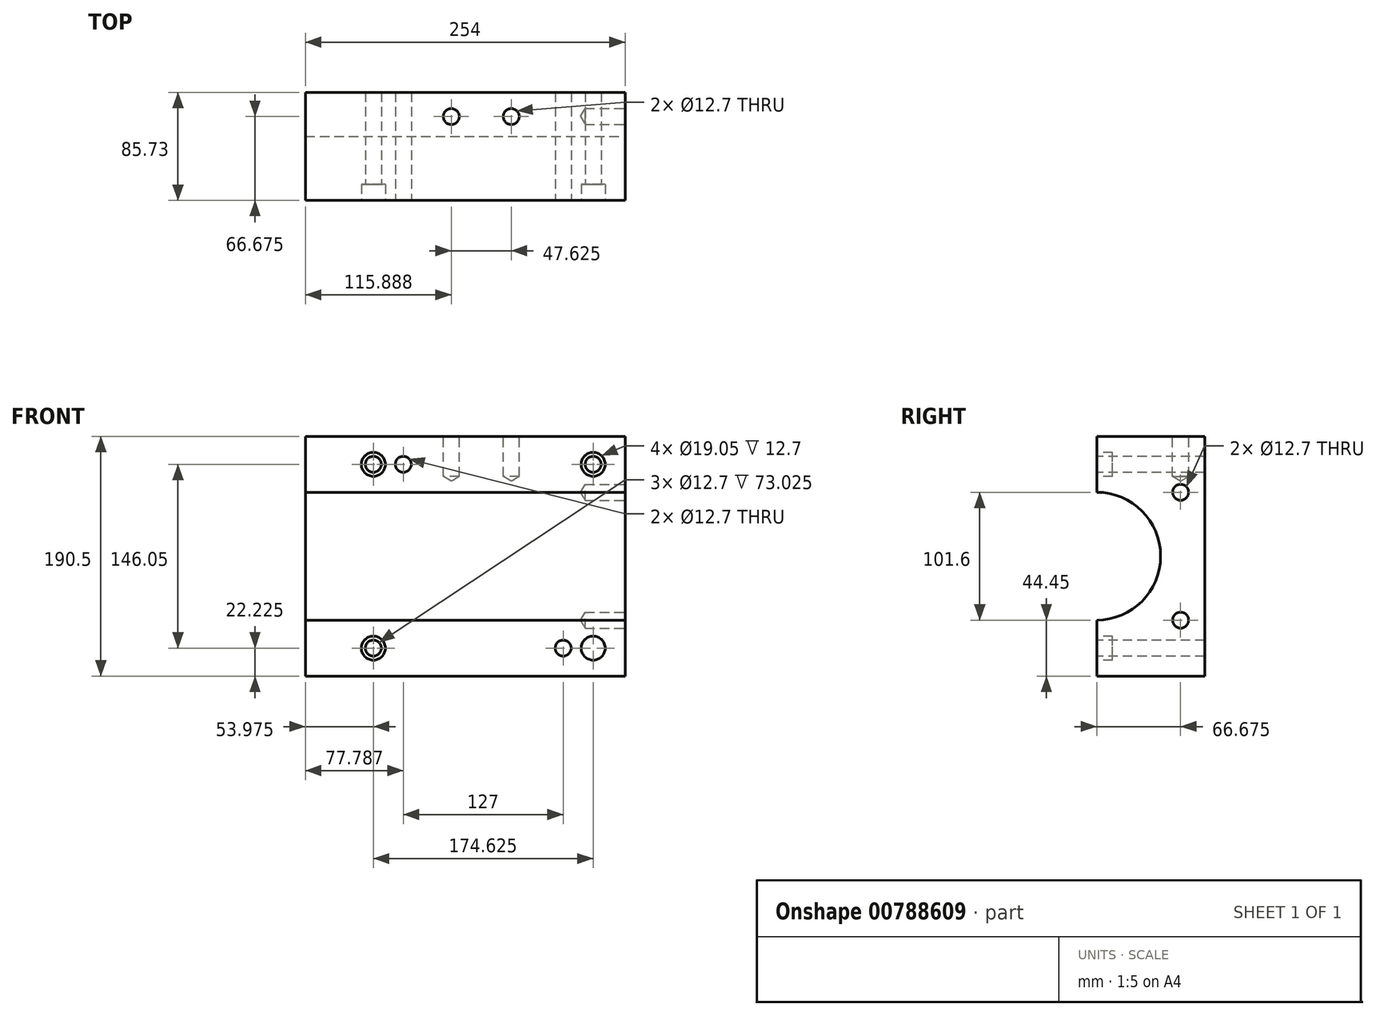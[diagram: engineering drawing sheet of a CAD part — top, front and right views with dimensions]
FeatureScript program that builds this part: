
annotation { "Feature Type Name" : "Feature", "Feature Type Description" : "" }
export const myFeature = defineFeature(function(context is Context, id is Id, definition is map)
    precondition{}
    {
        {
            var Q0;
            Q0=qCreatedBy(makeId("Front.planeOp"),FACE);
            var sketch = newSketch(context, id + "F0", { "sketchPlane" : qUnion([Q0])});
            skLineSegment(sketch, "E0.bottom", {"start": v(-127, 95.25) * mm, "end": v(127, 95.25) * mm});
            skLineSegment(sketch, "E0.top", {"start": v(-127, -95.25) * mm, "end": v(127, -95.25) * mm});
            skLineSegment(sketch, "E0.left", {"start": v(-127, 95.25) * mm, "end": v(-127, -95.25) * mm});
            skLineSegment(sketch, "E0.right", {"start": v(127, 95.25) * mm, "end": v(127, -95.25) * mm});
            skPoint(sketch, "E0.middle", {"position": v(0, 0) * mm});
            skSolve(sketch);
        }
        {
            var Q0;
            Q0 = qSketchRegion(id + "F0", true);
            extrude(context, id + "F1", {"entities" : qUnion([Q0]), "oppositeDirection" : true, "depth" : 85.72 * mm, "offsetDistance" : 25.4 * mm});
        }
        {
            var Q0;
            Q0=qCreatedBy(makeId("Right.planeOp"),FACE);
            var sketch = newSketch(context, id + "F2", { "sketchPlane" : qUnion([Q0])});
            skArc(sketch, "E1", {"start": v(0, -50.8) * mm, "mid": v(50.8, 0) * mm, "end": v(0, 50.8) * mm});
            skLineSegment(sketch, "E2", {"start": v(0, 0) * mm, "end": v(0, 50.8) * mm});
            skLineSegment(sketch, "E3", {"start": v(0, 0) * mm, "end": v(0, -50.8) * mm});
            skSolve(sketch);
        }
        {
            var Q0;
            Q0 = qSketchRegion(id + "F2", true);
            extrude(context, id + "F3", {"entities" : qUnion([Q0]), "operationType" : NewBodyOperationType.REMOVE, "endBound" : BoundingType.SYMMETRIC, "oppositeDirection" : true, "depth" : 254 * mm, "offsetDistance" : 25.4 * mm});
        }
        {
            var Q0;
            {var subQ0=sQuery(id+"F0.wireOp",EDGE,"E0.bottom");var subQ1=sQuery(id+"F0.wireOp",EDGE,"E0.right");var subQ2=sQuery(id+"F0.wireOp",EDGE,"E0.left");Q0=makeQuery(id+"F3.boolean.opBoolean","SPLIT",FACE,{"disambiguationData":[TD([makeQuery(id+"F1.opExtrude","SWEPT_FACE",FACE,{"disambiguationData":[OSD([subQ0])]})])],"derivedFrom":makeQuery(id+"F1.opExtrude","CAP_FACE",FACE,{"disambiguationData":[OSD([subQ0,sQuery(id+"F0.wireOp",EDGE,"E0.top"),subQ2,subQ1])],"isStart":true})});}
            var sketch = newSketch(context, id + "F4", { "sketchPlane" : qUnion([Q0])});
            skLineSegment(sketch, "E4", {"start": v(-127, 73.02) * mm, "end": v(-73.02, 73.02) * mm, "construction": true});
            skCircle(sketch, "E5", {"center": v(-73.02, 73.02) * mm, "radius": 9.53 * mm});
            skLineSegment(sketch, "E6", {"start": v(-73.02, 73.02) * mm, "end": v(-73.02, 95.25) * mm, "construction": true});
            skLineSegment(sketch, "E7", {"start": v(0, 0) * mm, "end": v(0, 137.12) * mm, "construction": true});
            skPoint(sketch, "E7.endSnap0", {"position": v(0, 50.8) * mm});
            skLineSegment(sketch, "E8", {"start": v(0, 0) * mm, "end": v(220.34, 0) * mm, "construction": true});
            skLineSegment(sketch, "E9", {"start": v(0, 0) * mm, "end": v(-211.05, 0) * mm, "construction": true});
            skLineSegment(sketch, "E10", {"start": v(0, 0) * mm, "end": v(0, -119.32) * mm, "construction": true});
            skCircle(sketch, "E11.MirrorC", {"center": v(-73.02, -73.02) * mm, "radius": 9.53 * mm});
            skLineSegment(sketch, "E12", {"start": v(127, 73.02) * mm, "end": v(111.13, 73.02) * mm, "construction": true});
            skCircle(sketch, "E13", {"center": v(101.6, 73.02) * mm, "radius": 9.53 * mm});
            skCircle(sketch, "E14.MirrorC", {"center": v(101.6, -73.02) * mm, "radius": 9.53 * mm});
            skSolve(sketch);
        }
        {
            var Q0;
            Q0 = qSketchRegion(id + "F4", true);
            extrude(context, id + "F5", {"entities" : qUnion([Q0]), "operationType" : NewBodyOperationType.REMOVE, "oppositeDirection" : true, "depth" : 12.7 * mm, "offsetDistance" : 25.4 * mm});
        }
        {
            var Q0;
            {var subQ0=sQuery(id+"F0.wireOp",EDGE,"E0.bottom");var subQ1=sQuery(id+"F0.wireOp",EDGE,"E0.right");var subQ2=sQuery(id+"F0.wireOp",EDGE,"E0.left");Q0=makeQuery(id+"F3.boolean.opBoolean","SPLIT",FACE,{"disambiguationData":[TD([makeQuery(id+"F1.opExtrude","SWEPT_FACE",FACE,{"disambiguationData":[OSD([subQ0])]})])],"derivedFrom":makeQuery(id+"F1.opExtrude","CAP_FACE",FACE,{"disambiguationData":[OSD([subQ0,sQuery(id+"F0.wireOp",EDGE,"E0.top"),subQ2,subQ1])],"isStart":true})});}
            var sketch = newSketch(context, id + "F6", { "sketchPlane" : qUnion([Q0])});
            skCircle(sketch, "E15", {"center": v(-49.21, 73.02) * mm, "radius": 6.35 * mm});
            skPoint(sketch, "E16.start.orphan", {"position": v(101.6, 73.02) * mm});
            skLineSegment(sketch, "E17", {"start": v(0, 0) * mm, "end": v(215.97, 0) * mm});
            skCircle(sketch, "E18.MirrorC", {"center": v(77.79, -73.02) * mm, "radius": 6.35 * mm});
            skSolve(sketch);
        }
        {
            var Q0;
            Q0 = qSketchRegion(id + "F6", true);
            extrude(context, id + "F7", {"entities" : qUnion([Q0]), "operationType" : NewBodyOperationType.REMOVE, "endBound" : BoundingType.UP_TO_NEXT, "oppositeDirection" : true, "depth" : 25.4 * mm, "offsetDistance" : 25.4 * mm});
        }
        {
            var Q0;
            Q0=makeQuery(id+"F5.boolean.opBoolean","COPY",FACE,{"derivedFrom":makeQuery(id+"F5.opExtrude","CAP_FACE",FACE,{"disambiguationData":[OSD([sQuery(id+"F4.wireOp",EDGE,"E5")])],"isStart":false})});
            var sketch = newSketch(context, id + "F8", { "sketchPlane" : qUnion([Q0])});
            skCircle(sketch, "E19", {"center": v(-73.02, 73.02) * mm, "radius": 6.35 * mm});
            skLineSegment(sketch, "E20", {"start": v(0, 0) * mm, "end": v(0, 114.26) * mm, "construction": true});
            skLineSegment(sketch, "E21", {"start": v(0, 0) * mm, "end": v(0, -112.48) * mm, "construction": true});
            skLineSegment(sketch, "E22", {"start": v(0, 0) * mm, "end": v(-162.05, 0) * mm, "construction": true});
            skLineSegment(sketch, "E23", {"start": v(0, 0) * mm, "end": v(231.12, 0) * mm, "construction": true});
            skCircle(sketch, "E24.MirrorC", {"center": v(-73.02, -73.02) * mm, "radius": 6.35 * mm});
            skSolve(sketch);
        }
        {
            var Q0;
            Q0=makeQuery(id+"F5.boolean.opBoolean","COPY",FACE,{"derivedFrom":makeQuery(id+"F5.opExtrude","CAP_FACE",FACE,{"disambiguationData":[OSD([sQuery(id+"F4.wireOp",EDGE,"E13")])],"isStart":false})});
            var sketch = newSketch(context, id + "F9", { "sketchPlane" : qUnion([Q0])});
            skCircle(sketch, "E25", {"center": v(101.6, 73.02) * mm, "radius": 6.35 * mm});
            skLineSegment(sketch, "E26", {"start": v(0, 0) * mm, "end": v(190.85, 0) * mm});
            skCircle(sketch, "E27.MirrorC", {"center": v(101.6, -73.02) * mm, "radius": 6.35 * mm});
            skSolve(sketch);
        }
        {
            var Q0;
            Q0 = qSketchRegion(id + "F8", true);
            var Q1;
            Q1=makeQuery(id+"F9.imprint","IMPRINT",FACE,{"disambiguationData":[TD([[makeQuery(id+"F9.imprint","IMPRINT",EDGE,{"derivedFrom":sQuery(id+"F9.wireOp",EDGE,"E25")}),1.0]])]});
            var Q2;
            Q2=makeQuery(id+"F9.imprint","IMPRINT",FACE,{"disambiguationData":[TD([[makeQuery(id+"F9.imprint","IMPRINT",EDGE,{"derivedFrom":sQuery(id+"F9.wireOp",EDGE,"E27.MirrorC")}),-1.0]])]});
            extrude(context, id + "F10", {"entities" : qUnion([Q0, Q1, Q2]), "operationType" : NewBodyOperationType.REMOVE, "oppositeDirection" : true, "depth" : 82.55 * mm, "offsetDistance" : 25.4 * mm});
        }
        {
            var Q0;
            Q0=makeQuery(id+"F1.opExtrude","SWEPT_FACE",FACE,{"disambiguationData":[OSD([sQuery(id+"F0.wireOp",EDGE,"E0.bottom")])]});
            var sketch = newSketch(context, id + "F11", { "sketchPlane" : qUnion([Q0])});
            skLineSegment(sketch, "E28", {"start": v(-127, 85.73) * mm, "end": v(-127, 76.2) * mm, "construction": true});
            skLineSegment(sketch, "E29", {"start": v(-127, 76.2) * mm, "end": v(-33.34, 76.2) * mm, "construction": true});
            skLineSegment(sketch, "E30", {"start": v(-33.34, 76.2) * mm, "end": v(-11.11, 76.2) * mm, "construction": true});
            skLineSegment(sketch, "E31", {"start": v(-11.11, 76.2) * mm, "end": v(-11.11, 66.68) * mm, "construction": true});
            skLineSegment(sketch, "E32", {"start": v(127, 85.73) * mm, "end": v(127, 76.2) * mm});
            skLineSegment(sketch, "E33", {"start": v(-11.11, 66.68) * mm, "end": v(36.51, 66.68) * mm, "construction": true});
            skSolve(sketch);
        }
        {
            var Q0;
            Q0=sQuery(id+"F11.wireOp",VERTEX,"E31.end");
            var Q1;
            Q1=sQuery(id+"F11.wireOp",VERTEX,"E33.end");
            var Q2;
            Q2=makeQuery(id+"F1.opExtrude","SWEPT_BODY",BODY,{"disambiguationData":[OSD([sQuery(id+"F0.wireOp",EDGE,"E0.bottom"),sQuery(id+"F0.wireOp",EDGE,"E0.top"),sQuery(id+"F0.wireOp",EDGE,"E0.left"),sQuery(id+"F0.wireOp",EDGE,"E0.right")])]});
            hole(context, id + "F12", {"style" : HoleStyle.SIMPLE, "endStyle" : HoleEndStyle.BLIND, "holeDiameter" : 12.7 * mm, "majorDiameter" : 5 * mm, "holeDepth" : 31.75 * mm, "isTappedThrough" : true, "tappedDepth" : 21.35 * mm, "tapClearance" : 13, "locations" : qUnion([Q0, Q1]), "scope" : qUnion([Q2])});
        }
        {
            var Q0;
            Q0=makeQuery(id+"F1.opExtrude","SWEPT_FACE",FACE,{"disambiguationData":[OSD([sQuery(id+"F0.wireOp",EDGE,"E0.right")])]});
            var sketch = newSketch(context, id + "F13", { "sketchPlane" : qUnion([Q0])});
            skLineSegment(sketch, "E34", {"start": v(85.73, 95.25) * mm, "end": v(66.68, 95.25) * mm, "construction": true});
            skLineSegment(sketch, "E35", {"start": v(66.68, 95.25) * mm, "end": v(66.68, 50.8) * mm, "construction": true});
            skLineSegment(sketch, "E36", {"start": v(85.73, -95.25) * mm, "end": v(66.68, -95.25) * mm, "construction": true});
            skLineSegment(sketch, "E37", {"start": v(66.68, -95.25) * mm, "end": v(66.68, -50.8) * mm, "construction": true});
            skSolve(sketch);
        }
        {
            var Q0;
            Q0=sQuery(id+"F13.wireOp",VERTEX,"E35.end");
            var Q1;
            Q1=sQuery(id+"F13.wireOp",VERTEX,"E37.end");
            var Q2;
            Q2=makeQuery(id+"F1.opExtrude","SWEPT_BODY",BODY,{"disambiguationData":[OSD([sQuery(id+"F0.wireOp",EDGE,"E0.bottom"),sQuery(id+"F0.wireOp",EDGE,"E0.top"),sQuery(id+"F0.wireOp",EDGE,"E0.left"),sQuery(id+"F0.wireOp",EDGE,"E0.right")])]});
            hole(context, id + "F14", {"style" : HoleStyle.SIMPLE, "endStyle" : HoleEndStyle.BLIND, "holeDiameter" : 12.7 * mm, "majorDiameter" : 6.35 * mm, "holeDepth" : 31.75 * mm, "isTappedThrough" : true, "tappedDepth" : 21.36 * mm, "tapClearance" : 3, "locations" : qUnion([Q0, Q1]), "scope" : qUnion([Q2])});
        }
    });
